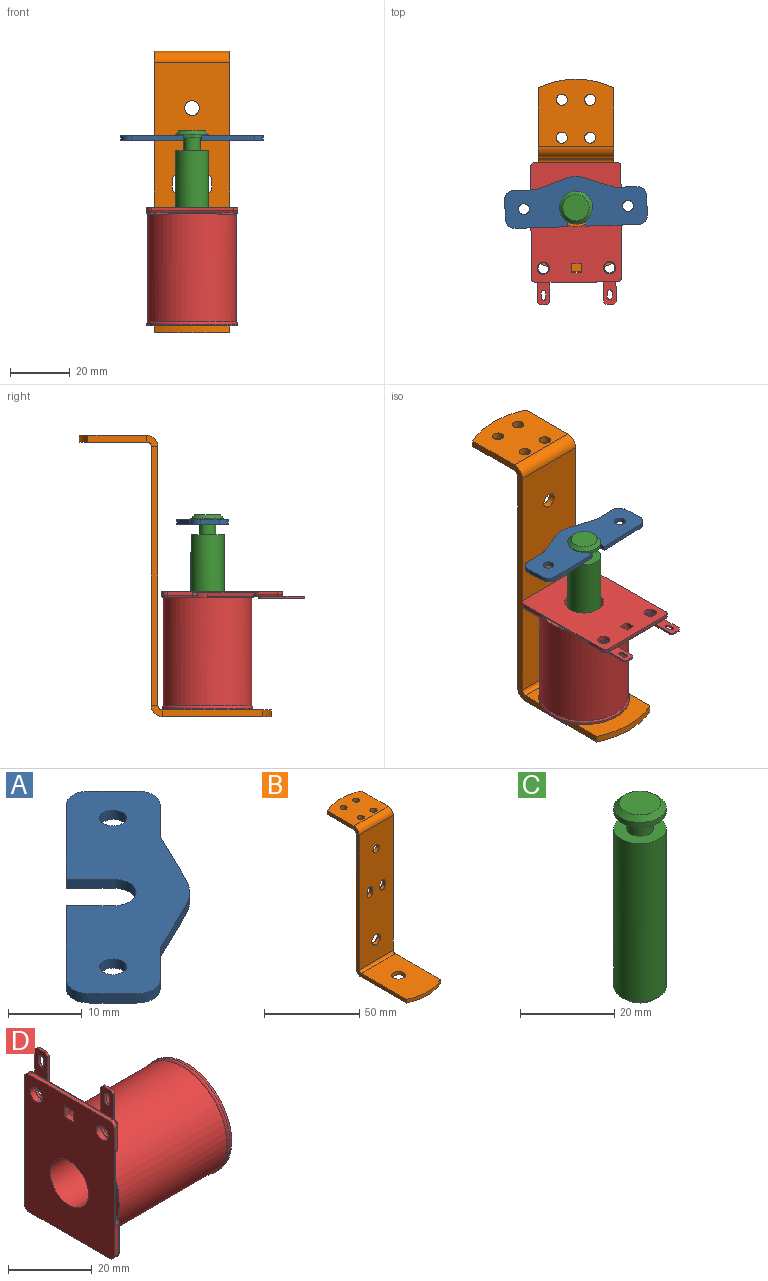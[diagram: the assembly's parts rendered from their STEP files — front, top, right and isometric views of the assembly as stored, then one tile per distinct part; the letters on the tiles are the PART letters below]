
ASSEMBLY  parts=4 mates=3
PART A: 22 faces, bbox 40x40x1.5 mm
  f0: plane 40.03x40.03mm, normal (0,0,1), area 579.5mm2, adj f2,f3,f4,f5,f6,f7,f8,f9
  f1: plane 40.03x40.03mm, normal (0,0,-1), area 579.5mm2, adj f2,f3,f4,f5,f6,f7,f8,f9
  f2: plane 4.49x4.49mm, normal (-0.71,-0.71,0), area 9.7mm2, adj f0,f1,f3,f13
  f3: cylinder r=3.11mm len=5.31mm, axis (0,0,-1), area 14.9mm2, adj f0,f1,f2,f4
  f4: plane 4.49x4.49mm, normal (0.71,0.71,0), area 9.7mm2, adj f0,f1,f3,f5
  f5: plane 12.39x12.39mm, normal (-0.71,0.71,0), area 26.7mm2, adj f0,f1,f4,f21
  f6: plane 4.49x4.49mm, normal (-0.71,-0.71,0), area 9.7mm2, adj f0,f1,f19,f21
  f7: plane 4.91x4.91mm, normal (0.71,-0.71,0), area 10.6mm2, adj f0,f1,f16,f19
  f8: plane 9.08x4.4mm, normal (0.44,-0.9,0), area 15.4mm2, adj f0,f1,f9,f16
  f9: cylinder r=9.53mm len=4.42mm, axis (0,0,-1), area 9.7mm2, adj f0,f1,f8,f10
  f10: plane 9.08x4.4mm, normal (0.9,-0.44,0), area 15.4mm2, adj f0,f1,f9,f17
  f11: plane 4.91x4.91mm, normal (0.71,-0.71,0), area 10.6mm2, adj f0,f1,f17,f18
  f12: plane 4.49x4.49mm, normal (0.71,0.71,0), area 9.7mm2, adj f0,f1,f18,f20
  f13: plane 12.39x12.39mm, normal (-0.71,0.71,0), area 26.7mm2, adj f0,f1,f2,f20
  f14: cylinder r=1.83mm len=3.66mm, axis (0,0,-1), area 17.5mm2, adj f0,f1
  f15: cylinder r=1.83mm len=3.66mm, axis (0,0,-1), area 17.5mm2, adj f0,f1
  f16: cylinder r=3.17mm len=1.52mm, axis (0,0,1), area 1.6mm2, adj f0,f1,f7,f8
  f17: cylinder r=3.17mm len=1.52mm, axis (0,0,1), area 1.6mm2, adj f0,f1,f10,f11
  f18: cylinder r=3.17mm len=4.49mm, axis (0,0,-1), area 7.6mm2, adj f0,f1,f11,f12
  f19: cylinder r=3.17mm len=4.49mm, axis (0,0,-1), area 7.6mm2, adj f0,f1,f6,f7
  f20: cylinder r=3.17mm len=4.49mm, axis (0,0,-1), area 7.6mm2, adj f0,f1,f12,f13
  f21: cylinder r=3.17mm len=4.49mm, axis (0,0,-1), area 7.6mm2, adj f0,f1,f5,f6
PART B: 37 faces, bbox 25.4x64.4x94.4 mm
  f0: plane 36.53x25.4mm, normal (0,0,1), area 863.5mm2, adj f2,f3,f19,f21,f22
  f1: plane 36.53x25.4mm, normal (0,0,-1), area 863.5mm2, adj f2,f3,f14,f21,f22
  f2: plane 33.6x2.26mm, normal (-1,0,0), area 76mm2, adj f0,f1,f13,f21
  f3: plane 33.6x2.26mm, normal (1,0,0), area 76mm2, adj f0,f1,f11,f21
  f4: plane 25.4x22.56mm, normal (0,0,-1), area 505.9mm2, adj f6,f7,f16,f20,f23,f24,f25,f26
  f5: plane 25.4x22.56mm, normal (0,0,1), area 505.9mm2, adj f6,f7,f17,f20,f23,f24,f25,f26
  f6: plane 19.69x2.26mm, normal (1,0,0), area 44.5mm2, adj f4,f5,f8,f20
  f7: plane 19.69x2.26mm, normal (-1,0,0), area 44.5mm2, adj f4,f5,f9,f20
  f8: plane 3.78x3.78mm, normal (1,0,0), area 9.4mm2, adj f6,f12,f16,f17
  f9: plane 3.78x3.78mm, normal (-1,0,0), area 9.4mm2, adj f7,f10,f16,f17
  f10: plane 86.79x2.26mm, normal (-1,0,0), area 196.2mm2, adj f9,f13,f15,f18
  f11: plane 3.78x3.78mm, normal (1,0,0), area 9.4mm2, adj f3,f12,f14,f19
  f12: plane 86.79x2.26mm, normal (1,0,0), area 196.2mm2, adj f8,f11,f15,f18
  f13: plane 3.78x3.78mm, normal (-1,0,0), area 9.4mm2, adj f2,f10,f14,f19
  f14: cylinder r=3.78mm len=25.4mm, axis (-1,0,0), area 151mm2, adj f1,f11,f13,f15
  f15: plane 86.79x25.4mm, normal (0,1,0), area 2108.7mm2, adj f10,f12,f14,f16,f27,f28,f29,f30
  f16: cylinder r=1.52mm len=25.4mm, axis (-1,0,0), area 60.8mm2, adj f4,f8,f9,f15
  f17: cylinder r=3.78mm len=25.4mm, axis (-1,0,0), area 151mm2, adj f5,f8,f9,f18
  f18: plane 86.79x25.4mm, normal (0,-1,0), area 2108.7mm2, adj f10,f12,f17,f19,f27,f28,f29,f30
  f19: cylinder r=1.52mm len=25.4mm, axis (-1,0,0), area 60.8mm2, adj f0,f11,f13,f18
  f20: cylinder r=29.53mm len=25.4mm, axis (0,0,-1), area 59.4mm2, adj f4,f5,f6,f7
  f21: cylinder r=29.07mm len=25.4mm, axis (0,0,-1), area 59.4mm2, adj f0,f1,f2,f3
  f22: cylinder r=3.57mm len=7.14mm, axis (0,0,1), area 50.7mm2, adj f0,f1
  f23: cylinder r=1.85mm len=3.71mm, axis (0,0,1), area 26.3mm2, adj f4,f5
  f24: cylinder r=1.85mm len=3.71mm, axis (0,0,1), area 26.3mm2, adj f4,f5
  f25: cylinder r=1.85mm len=3.71mm, axis (0,0,1), area 26.3mm2, adj f4,f5
  f26: cylinder r=1.85mm len=3.71mm, axis (0,0,1), area 26.3mm2, adj f4,f5
  f27: cylinder r=2.45mm len=4.9mm, axis (0,-1,0), area 34.8mm2, adj f15,f18
  f28: cylinder r=3.25mm len=6.5mm, axis (0,-1,0), area 46.2mm2, adj f15,f18
  f29: cylinder r=1.91mm len=3.81mm, axis (0,-1,0), area 13.5mm2, adj f15,f18,f30,f32
  f30: plane 2.74x2.26mm, normal (-1,0,0), area 6.2mm2, adj f15,f18,f29,f31
  f31: cylinder r=1.91mm len=3.81mm, axis (0,-1,0), area 13.5mm2, adj f15,f18,f30,f32
  f32: plane 2.74x2.26mm, normal (1,0,0), area 6.2mm2, adj f15,f18,f29,f31
  f33: cylinder r=1.91mm len=3.81mm, axis (0,-1,0), area 13.5mm2, adj f15,f18,f34,f36
  f34: plane 2.74x2.26mm, normal (-1,0,0), area 6.2mm2, adj f15,f18,f33,f35
  f35: cylinder r=1.91mm len=3.81mm, axis (0,-1,0), area 13.5mm2, adj f15,f18,f34,f36
  f36: plane 2.74x2.26mm, normal (1,0,0), area 6.2mm2, adj f15,f18,f33,f35
PART C: 9 faces, bbox 11.1x11.1x48.8 mm
  f0: cylinder r=5.54mm len=41.02mm, axis (0,0,-1), area 1427.2mm2, adj f2,f3
  f1: plane 8.79x8.79mm, normal (0,0,-1), area 60.7mm2, adj f2
  f2: cone r=5.54mm half-angle=45deg, axis (0,0,1), area 50.4mm2, adj f0,f1
  f3: plane 11.07x11.07mm, normal (0,0,1), area 71.1mm2, adj f0,f5
  f4: plane 11.07x11.07mm, normal (0,0,-1), area 71.1mm2, adj f5,f8
  f5: cylinder r=2.83mm len=5.66mm, axis (0,0,-1), area 75.9mm2, adj f3,f4
  f6: plane 8.79x8.79mm, normal (0,0,1), area 60.7mm2, adj f7
  f7: cone r=4.39mm half-angle=45deg, axis (0,0,-1), area 50.4mm2, adj f6,f8
  f8: cylinder r=5.54mm len=11.07mm, axis (0,0,-1), area 44.2mm2, adj f4,f7
PART D: 102 faces, bbox 39.7x32.9x48.9 mm
  f0: plane 15.43x5.59mm, normal (1,0,0), area 57.5mm2, adj f85,f86,f87,f88,f89,f90,f91,f92
  f1: plane 8x4.19mm, normal (-1,0,0), area 28.2mm2, adj f40,f90,f91,f92,f94,f95,f96,f97
  f2: plane 29.29x9.35mm, normal (1,0,0), area 172.4mm2, adj f26,f29,f30,f31,f32,f35,f36,f37
  f3: cylinder r=7.24mm len=4.38mm, axis (-1,0,0), area 5.9mm2, adj f19,f20,f23,f24,f50,f57,f60
  f4: plane 12.19x10.36mm, normal (1,0,0), area 41.1mm2, adj f46,f47,f48,f49,f61
  f5: plane 12.19x12.01mm, normal (1,0,0), area 41.5mm2, adj f44,f45,f46,f61
  f6: plane 29.25x12.55mm, normal (1,0,0), area 74.5mm2, adj f44,f53,f54,f55,f56,f61
  f7: plane 37.13x1.47mm, normal (0,-1,0), area 29.2mm2, adj f8,f15,f16,f23,f33,f34,f38,f48
  f8: plane 40.18x30.3mm, normal (-1,0,0), area 1047.8mm2, adj f7,f9,f10,f11,f12,f13,f14,f15
  f9: plane 37.13x1.47mm, normal (0,1,0), area 51.5mm2, adj f8,f13,f14,f42,f43,f44
  f10: plane 27.25x1.09mm, normal (0,0,1), area 29.8mm2, adj f8,f14,f16,f40
  f11: plane 27.25x1.47mm, normal (0,0,-1), area 40.2mm2, adj f8,f13,f15,f46
  f12: cylinder r=6.48mm len=39.69mm, axis (-1,0,0), area 1615.1mm2, adj f8,f17
  f13: cylinder r=1.52mm len=1.52mm, axis (-1,0,0), area 3.5mm2, adj f8,f9,f11,f45
  f14: cylinder r=1.52mm len=1.52mm, axis (-1,0,0), area 2.6mm2, adj f8,f9,f10,f41
  f15: cylinder r=1.52mm len=1.52mm, axis (-1,0,0), area 3.5mm2, adj f7,f8,f11,f47
  f16: cylinder r=1.52mm len=1.52mm, axis (-1,0,0), area 2.6mm2, adj f7,f8,f10,f39
  f17: plane 30.38x30.38mm, normal (1,0,0), area 593mm2, adj f12,f18
  f18: cylinder r=15.19mm len=30.38mm, axis (1,0,0), area 60.6mm2, adj f17,f58
  f19: plane 7.35x1.04mm, normal (0,0,1), area 7.7mm2, adj f3,f23,f33,f50
  f20: plane 15.47x3.39mm, normal (0,-0.98,-0.21), area 18.1mm2, adj f3,f21,f22,f23,f26
  f21: plane 3x0.66mm, normal (0,0,-1), area 2mm2, adj f20,f23,f34,f36
  f22: plane 15.47x7.62mm, normal (-1,0,0), area 57.2mm2, adj f20,f24,f25,f26
  f23: plane 22.12x8.87mm, normal (1,0,0), area 126.8mm2, adj f3,f7,f19,f20,f21,f33,f34
  f24: plane 6.59x2.26mm, normal (0,-0.32,-0.95), area 1.1mm2, adj f3,f22,f25,f57
  f25: cylinder r=1.52mm len=1.97mm, axis (-1,0,0), area 0.4mm2, adj f22,f24,f26,f56
  f26: plane 11.75x4.33mm, normal (0,-0.94,0.35), area 1.8mm2, adj f2,f20,f22,f25,f36,f51,f55
  f27: cylinder r=2.03mm len=4.06mm, axis (-1,0,0), area 20.4mm2, adj f8,f84
  f28: cylinder r=2.03mm len=4.06mm, axis (-1,0,0), area 20.4mm2, adj f8,f64
  f29: plane 3.18x1.6mm, normal (0,1,0), area 5.1mm2, adj f2,f8,f30,f32
  f30: plane 3.18x1.6mm, normal (0,0,1), area 5.1mm2, adj f2,f8,f29,f31
  f31: plane 3.18x1.6mm, normal (0,-1,0), area 5.1mm2, adj f2,f8,f30,f32
  f32: plane 3.18x1.6mm, normal (0,0,-1), area 5.1mm2, adj f2,f8,f29,f31
  f33: cylinder r=1.52mm len=1.52mm, axis (-1,0,0), area 2.5mm2, adj f7,f19,f23,f49
  f34: cylinder r=1.52mm len=1.52mm, axis (-1,0,0), area 1.6mm2, adj f7,f21,f23,f37
  f35: plane 24.92x0.13mm, normal (0,0,1), area 3.2mm2, adj f2,f43,f51,f53
  f36: cylinder r=0.51mm len=3.18mm, axis (0,1,0), area 2.4mm2, adj f2,f21,f26,f37
  f37: torus R=1.02mm, axis (-1,0,0), area 1.7mm2, adj f2,f34,f36,f38
  f38: cylinder r=0.51mm len=6.48mm, axis (0,0,1), area 5.2mm2, adj f2,f7,f37,f39
  f39: torus R=1.02mm, axis (-1,0,0), area 1.7mm2, adj f2,f16,f38,f40
  f40: cylinder r=0.51mm len=27.25mm, axis (0,1,0), area 21.7mm2, adj f1,f2,f10,f39,f41,f66
  f41: torus R=1.02mm, axis (-1,0,0), area 1.7mm2, adj f2,f14,f40,f42
  f42: cylinder r=0.51mm len=8.51mm, axis (0,0,-1), area 6.5mm2, adj f2,f9,f41,f43
  f43: cylinder r=0.51mm len=0.64mm, axis (1,0,0), area 0.2mm2, adj f9,f35,f42,f52
  f44: cylinder r=0.51mm len=28.88mm, axis (0,0,1), area 23mm2, adj f5,f6,f9,f45,f52,f59
  f45: torus R=1.02mm, axis (-1,0,0), area 1.7mm2, adj f5,f13,f44,f46
  f46: cylinder r=0.51mm len=27.25mm, axis (0,1,0), area 21.7mm2, adj f4,f5,f11,f45,f47,f62
  f47: torus R=1.02mm, axis (-1,0,0), area 1.7mm2, adj f4,f15,f46,f48
  f48: cylinder r=0.51mm len=8.53mm, axis (0,0,-1), area 6.8mm2, adj f4,f7,f47,f49
  f49: torus R=1.02mm, axis (-1,0,0), area 1.7mm2, adj f4,f33,f48,f50,f60
  f50: cylinder r=0.51mm len=7.67mm, axis (0,-1,0), area 6mm2, adj f3,f19,f49,f60
  f51: cylinder r=0.51mm len=0.48mm, axis (-1,0,0), area 0.1mm2, adj f2,f26,f35,f54
  f52: bspline ~0.61x0.51mm, area 0.2mm2, adj f43,f44,f53
  f53: cylinder r=0.25mm len=24.92mm, axis (0,1,0), area 9.9mm2, adj f6,f35,f52,f54
  f54: torus R=0.25mm, axis (-1,0,0), area 0.2mm2, adj f6,f51,f53,f55
  f55: cylinder r=0.25mm len=11mm, axis (0,-0.35,-0.94), area 4.6mm2, adj f6,f26,f54,f56
  f56: torus R=1.27mm, axis (-1,0,0), area 0.9mm2, adj f6,f25,f55,f57,f60
  f57: cylinder r=0.25mm len=6.68mm, axis (0,0.95,-0.32), area 2.8mm2, adj f3,f24,f56,f60
  f58: torus R=14.43mm, axis (1,0,0), area 112.2mm2, adj f18,f63
  f59: plane 5.34x0.24mm, normal (-1,0,0), area 0.9mm2, adj f44,f61
  f60: plane 8.93x7.57mm, normal (-1,0,0), area 44.3mm2, adj f3,f49,f50,f56,f57,f61
  f61: cylinder r=14.88mm len=36.31mm, axis (-1,0,0), area 3395.7mm2, adj f4,f5,f6,f59,f60,f62,f63
  f62: plane 4.9x0.2mm, normal (-1,0,0), area 0.7mm2, adj f46,f61
  f63: plane 29.77x29.77mm, normal (1,0,0), area 42.1mm2, adj f58,f61
  f64: plane 4.06x4.06mm, normal (-1,0,0), area 2.8mm2, adj f28,f75
  f65: plane 15.43x5.59mm, normal (1,0,0), area 57.5mm2, adj f67,f68,f69,f70,f71,f72,f73,f74
  f66: plane 8x4.19mm, normal (-1,0,0), area 28.2mm2, adj f40,f68,f69,f70,f76,f77,f78,f79
  f67: plane 0.7x0.64mm, normal (0,0,1), area 0.4mm2, adj f2,f65,f68,f74
  f68: plane 8.32x0.64mm, normal (0,1,0), area 5.3mm2, adj f2,f65,f66,f67,f82
  f69: plane 2.67x0.64mm, normal (0,0,1), area 1.7mm2, adj f65,f66,f82,f83
  f70: plane 8.32x0.64mm, normal (0,-1,0), area 5.3mm2, adj f2,f65,f66,f71,f83
  f71: plane 0.7x0.64mm, normal (0,0,1), area 0.4mm2, adj f2,f65,f70,f72
  f72: plane 5.59x0.64mm, normal (0,-1,0), area 3.5mm2, adj f2,f65,f71,f81
  f73: plane 4.06x0.64mm, normal (0,0,-1), area 2.6mm2, adj f2,f65,f80,f81
  f74: plane 5.59x0.64mm, normal (0,1,0), area 3.5mm2, adj f2,f65,f67,f80
  f75: cylinder r=1.8mm len=3.6mm, axis (-1,0,0), area 7.2mm2, adj f64,f65
  f76: cylinder r=0.81mm len=1.62mm, axis (1,0,0), area 1.6mm2, adj f65,f66,f77,f79
  f77: plane 1.64x0.64mm, normal (0,-1,0), area 1mm2, adj f65,f66,f76,f78
  f78: cylinder r=0.81mm len=1.62mm, axis (1,0,0), area 1.6mm2, adj f65,f66,f77,f79
  f79: plane 1.64x0.64mm, normal (0,1,0), area 1mm2, adj f65,f66,f76,f78
  f80: plane 0.76x0.76mm, normal (0,0.71,-0.71), area 0.7mm2, adj f2,f65,f73,f74
  f81: plane 0.76x0.76mm, normal (0,-0.71,-0.71), area 0.7mm2, adj f2,f65,f72,f73
  f82: plane 0.76x0.76mm, normal (0,0.71,0.71), area 0.7mm2, adj f65,f66,f68,f69
  f83: plane 0.76x0.76mm, normal (0,-0.71,0.71), area 0.7mm2, adj f65,f66,f69,f70
  f84: plane 4.06x4.06mm, normal (-1,0,0), area 2.8mm2, adj f27,f93
  f85: plane 0.7x0.64mm, normal (0,0,1), area 0.4mm2, adj f0,f2,f86,f92
  f86: plane 5.59x0.64mm, normal (0,-1,0), area 3.5mm2, adj f0,f2,f85,f98
  f87: plane 4.06x0.64mm, normal (0,0,-1), area 2.6mm2, adj f0,f2,f98,f99
  f88: plane 5.59x0.64mm, normal (0,1,0), area 3.5mm2, adj f0,f2,f89,f99
  f89: plane 0.7x0.64mm, normal (0,0,1), area 0.4mm2, adj f0,f2,f88,f90
  f90: plane 8.32x0.64mm, normal (0,1,0), area 5.3mm2, adj f0,f1,f2,f89,f101
  f91: plane 2.67x0.64mm, normal (0,0,1), area 1.7mm2, adj f0,f1,f100,f101
  f92: plane 8.32x0.64mm, normal (0,-1,0), area 5.3mm2, adj f0,f1,f2,f85,f100
  f93: cylinder r=1.8mm len=3.6mm, axis (-1,0,0), area 7.2mm2, adj f0,f84
  f94: cylinder r=0.81mm len=1.62mm, axis (1,0,0), area 1.6mm2, adj f0,f1,f95,f97
  f95: plane 1.64x0.64mm, normal (0,-1,0), area 1mm2, adj f0,f1,f94,f96
  f96: cylinder r=0.81mm len=1.62mm, axis (1,0,0), area 1.6mm2, adj f0,f1,f95,f97
  f97: plane 1.64x0.64mm, normal (0,1,0), area 1mm2, adj f0,f1,f94,f96
  f98: plane 0.76x0.76mm, normal (0,-0.71,-0.71), area 0.7mm2, adj f0,f2,f86,f87
  f99: plane 0.76x0.76mm, normal (0,0.71,-0.71), area 0.7mm2, adj f0,f2,f87,f88
  f100: plane 0.76x0.76mm, normal (0,-0.71,0.71), area 0.7mm2, adj f0,f1,f91,f92
  f101: plane 0.76x0.76mm, normal (0,0.71,0.71), area 0.7mm2, adj f0,f1,f90,f91
PLACE A rot(axis=(0,0,1),136.8deg) t=(-7.66,-29.25,40.68)mm
PLACE B t=(-7.66,-12.61,22.57)mm fixed
PLACE C t=(-7.66,-29.25,39.92)mm
PLACE D rot(axis=(0.58,0.58,-0.58),119.7deg) t=(-7.66,-29.25,-29.84)mm
MATE revolute D.f3 <-> B.f22  axis (0,0,-1) through (-7.66,-29.25,-69.53)mm
MATE revolute C.f0 <-> A.f3  axis (0,0,-1) through (-7.66,-29.25,-6.46)mm
MATE revolute C.f0 <-> B.f22  axis (0,0,-1) through (-7.66,-29.25,-51.75)mm
